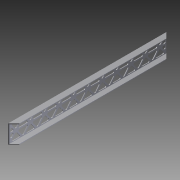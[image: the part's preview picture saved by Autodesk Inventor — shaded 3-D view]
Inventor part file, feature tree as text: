
AUTODESK INVENTOR PART (.ipt)
format: ipt  version: 2012 (Build 160160000, 160)  size: 557,568 bytes
history: native  units: in
note: dims shown in document units (in); Inventor stores cm internally (conversion verified against a paired STEP export)
features: extrude x3, sketch x3, fillet x1
ambient origin geometry x8: Origin, YZ Plane, XZ Plane, XY Plane, X Axis, Y Axis, Z Axis, Center Point
bodies: Solid1 (feature_tree)
feature tree (7):
  extrude  "Extrusion1"  Depth=1.0in
  extrude  "Extrusion2"  Depth=0.125in
  extrude  "Extrusion3"  Depth=0.125in
  fillet  "Fillet1"  Radius=28.0in
  sketch  "Sketch1"  dims[d0=3.25in d1=1.0in]
  sketch  "Sketch2"  dims[d2=1.0in d3=0.125in]
  sketch  "Sketch3"  dims[d4=0.125in d5=0.125in d6=28.0in d7=0.0in d8=45.0deg d9=1.0in d10=0.0in d11=0.5232in d12=0.2616in d13=0.25in d14=0.125in d15=0.125in d16=0.125in d17=0.125in d18=0.25in d19=0.125in d20=0.125in d21=0.25in d22=0.125in d23=0.125in d24=0.25in d25=0.125in d26=0.125in d27=0.125in d28=0.125in d29=0.125in d30=0.125in d31=0.125in d32=0.25in d34=2.5455in d35=3.937in d37=2.5455in d38=0.3937in d40=1.0in d42=0.125in d43=0.125in d44=0.125in d45=0.125in d46=0.25in d47=0.125in d48=0.125in d49=0.25in d50=0.125in d51=0.25in d52=0.125in d53=0.25in d54=1.0in d55=0.0in d56=0.1875in]
